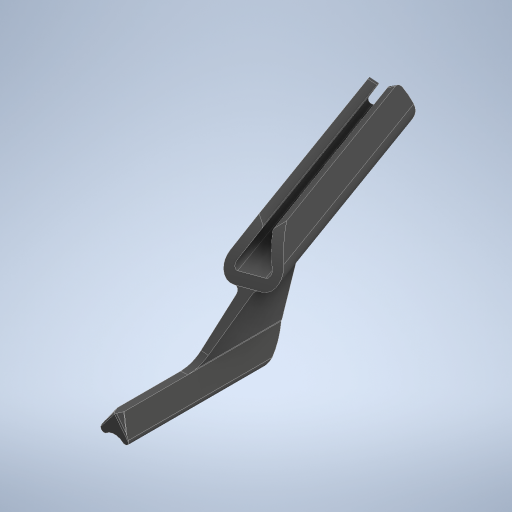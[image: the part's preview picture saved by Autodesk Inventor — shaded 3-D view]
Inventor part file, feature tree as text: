
AUTODESK INVENTOR PART (.ipt)
format: ipt  version: 2024 (Build 280153000, 153)  size: 813,568 bytes
history: native  units: in
note: dims shown in document units (in); Inventor stores cm internally (conversion verified against a paired STEP export)
features: extrude x15, other x15, plane x9, fillet x9, sketch x5, loft x1, mirror x1
ambient origin geometry x8: Origin, YZ Plane, XZ Plane, XY Plane, X Axis, Y Axis, Z Axis, Center Point
bodies: Solid2 (feature_tree), Body_sk1 (feature_tree), Body_sk2 (feature_tree)
feature tree (55):
  extrude  "Extrusion24"  Depth=0.0394in
  extrude  "Extrusion31"  Depth=0.426in
  plane  "Work Plane7"
  other  "Work Point1"
  other  "Work Point2"
  other  "Work Axis2"
  other  "Work Point3"
  plane  "Work Plane9"
  extrude  "Extrusion25"  TaperAngle=0.0deg  [1 undecoded]
  extrude  "Extrusion26"  Depth=0.0394in
  plane  "Work Plane8"
  other  "Grip_sketch"
  extrude  "Extrusion27"  Depth=0.1181in
  extrude  "Extrusion28"  Depth=0.063in
  fillet  "Fillet7"  Radius=2.7559in
  fillet  "Fillet8"  Radius=1.1811in
  other  "Bridge_sketch_upper"
  plane  "Work Plane10"
  other  "Bridge_sketck_lower"
  loft  "Loft1"
  extrude  "Extrusion30"  Depth=0.1181in
  extrude  "Extrusion36"  Depth=0.1181in
  fillet  "Fillet11"  Radius=0.0709in
  extrude  "Extrusion37"  Depth=0.5906in
  fillet  "Fillet12"  Radius=0.1181in
  fillet  "Fillet13"  Radius=0.3543in
  extrude  "Shorten_ex"  Depth=0.1181in
  other  "Work Point4"
  other  "Work Point5"
  plane  "Work Plane11"
  plane  "Work Plane12"
  extrude  "Extrusion33"  Depth=0.1181in
  other  "Work Point6"
  plane  "Work Plane13"
  sketch  "Sketch12"  dims[d181=1.9685in d182=0.0in d183=0.0in]
  extrude  "Extrusion34"  Depth=0.0787in TaperAngle=0.0deg
  extrude  "Extrusion35"  Depth=0.0394in
  fillet  "Fillet14"  Radius=0.0394in
  plane  "Work Plane15"
  extrude  "Extrusion38"  Depth=0.0394in
  plane  "Work Plane16"
  extrude  "Extrusion39"  Depth=0.0709in TaperAngle=0.0deg
  fillet  "Fillet15"  Radius=0.0197in
  fillet  "Fillet16"  Radius=0.0197in
  mirror  "Mirror4"
  fillet  "Fillet10"  Radius=0.063in
  other  "Work Axis1"
  other  "Work Axis3"
  other  "Work Axis4"
  other  "Work Axis5"
  sketch  "Sketch10"  dims[d176=0.0394in d177=0.0394in]
  other  "Work Axis6"
  sketch  "Sketch11"  dims[d178=0.315in d180=0.426in]
  sketch  "Sketch13"  dims[d197=0.0472in d198=0.0394in]
  sketch  "Sketch14"  dims[d199=30.0deg d200=0.1181in d201=0.063in d202=2.7559in d203=0.0in d204=1.1811in d205=0.0in d206=0.0in d208=0.1181in d209=0.1181in d210=0.0709in d211=0.5906in d212=0.1181in d213=0.1181in d214=0.0709in d215=0.3543in d216=0.1181in d217=0.1181in d218=0.0709in d219=0.1181in d224=0.0787in d225=0.0in d227=0.0394in d228=0.0394in d229=0.0394in d230=0.0709in d231=0.0in d232=0.0197in d233=0.0197in d236=0.063in d237=0.4724in d238=0.8661in d242=0.1374in d243=0.5512in d244=0.2362in d246=0.0394in d247=1.2598in d248=0.0in d249=90.0deg d250=0.0in d251=90.0deg d252=0.0787in d253=0.0in d254=0.0787in d255=0.7874in d256=0.0in d257=0.2362in d258=0.0in d259=0.0in d260=0.0787in d261=0.1575in d262=0.0787in d263=0.7874in d264=0.3937in d265=0.7874in d266=0.0in d267=45.0deg d268=0.315in d269=0.2362in d270=0.1575in d271=0.3937in d272=0.3937in d273=0.0in d274=90.0deg d275=0.2362in d276=0.3937in d277=0.4724in d278=0.315in d279=0.7874in d280=0.0in d281=0.7874in d282=0.0in d283=0.2362in d284=0.2362in d285=0.7874in d286=0.0in d287=0.0197in d288=0.1227in d289=0.1249in d290=0.0394in d291=0.0in d292=0.0333in d293=0.0047in d294=0.0in d295=-0.1374in d296=0.1575in d297=0.1772in d298=0.1969in d299=0.0in d300=30.0deg d301=0.1181in d302=0.126in d303=0.0039in d304=0.1969in d305=0.0in d306=0.0079in d307=0.0394in d308=0.0472in d129=0.0in d130=0.0in d131=0.0in d132=0.0in d158=0.0197in d159=0.0344in d160=0.0197in d161=0.0344in]
note: 1 required parameter value undecoded (feature->parameter linkage not recoverable at this tier; creation-order binding heuristic only, values carry confidence <= 0.55)
